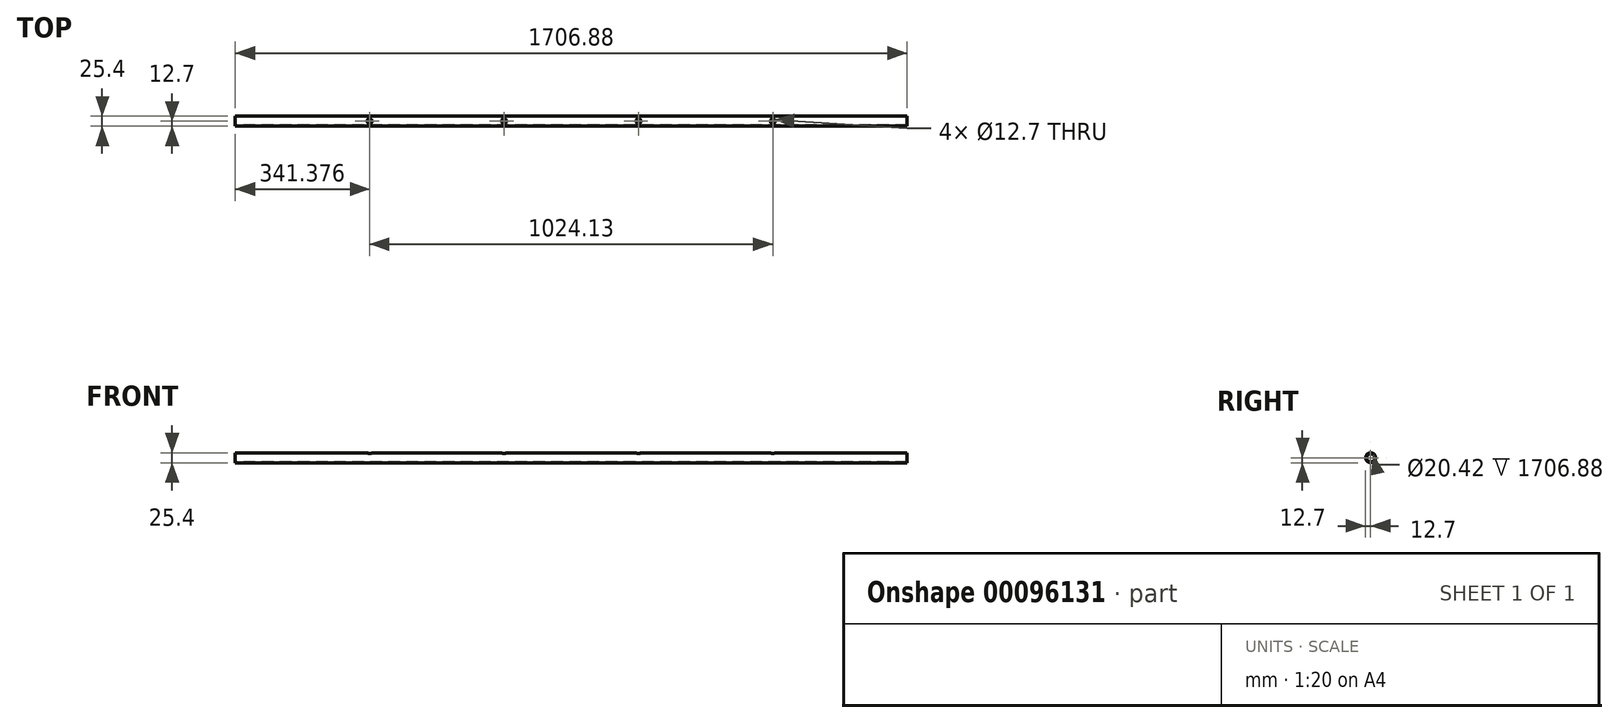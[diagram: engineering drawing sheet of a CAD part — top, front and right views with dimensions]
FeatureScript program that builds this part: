
annotation { "Feature Type Name" : "Feature", "Feature Type Description" : "" }
export const myFeature = defineFeature(function(context is Context, id is Id, definition is map)
    precondition{}
    {
        {
            var Q0;
            Q0=qCreatedBy(makeId("Right.planeOp"),FACE);
            var sketch = newSketch(context, id + "F0", { "sketchPlane" : qUnion([Q0])});
            skCircle(sketch, "E0", {"center": v(0, 0) * mm, "radius": 12.7 * mm});
            skCircle(sketch, "E1", {"center": v(0, 0) * mm, "radius": 10.21 * mm});
            skSolve(sketch);
        }
        {
            var Q0;
            Q0=makeQuery(id+"F0.imprint","IMPRINT",FACE,{"disambiguationData":[TD([[makeQuery(id+"F0.imprint","IMPRINT",EDGE,{"derivedFrom":sQuery(id+"F0.wireOp",EDGE,"E0")}),1.0]])]});
            extrude(context, id + "F1", {"entities" : qUnion([Q0]), "depth" : 1706.88 * mm});
        }
        {
            var Q0;
            Q0=qCreatedBy(makeId("Top.planeOp"),FACE);
            var sketch = newSketch(context, id + "F2", { "sketchPlane" : qUnion([Q0])});
            skCircle(sketch, "E2", {"center": v(341.38, 0) * mm, "radius": 6.35 * mm});
            skCircle(sketch, "E3", {"center": v(682.75, 0) * mm, "radius": 6.35 * mm});
            skCircle(sketch, "E4", {"center": v(1024.13, 0) * mm, "radius": 6.35 * mm});
            skCircle(sketch, "E5", {"center": v(1365.5, 0) * mm, "radius": 6.35 * mm});
            skSolve(sketch);
        }
        {
            var Q0;
            Q0=qSketchRegion(id+"F2",true);
            extrude(context, id + "F3", {"entities" : qUnion([Q0]), "operationType" : NewBodyOperationType.REMOVE, "depth" : 25.4 * mm});
        }
    });
